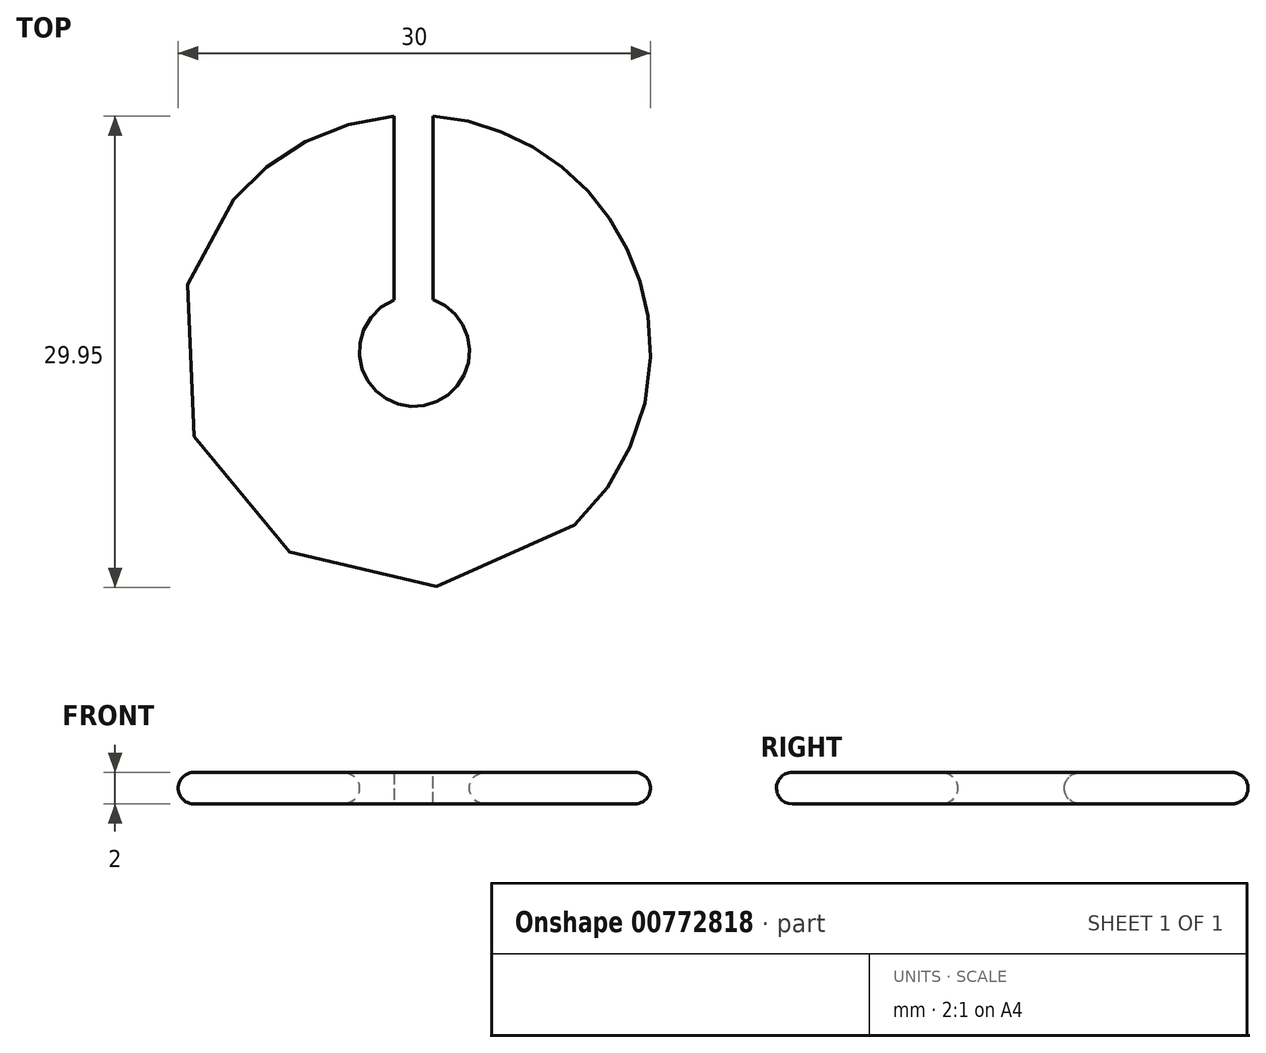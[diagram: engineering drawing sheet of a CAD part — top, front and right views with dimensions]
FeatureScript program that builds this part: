
annotation { "Feature Type Name" : "Feature", "Feature Type Description" : "" }
export const myFeature = defineFeature(function(context is Context, id is Id, definition is map)
    precondition{}
    {
        {
            var Q0;
            Q0=qCreatedBy(makeId("Top.planeOp"),FACE);
            var sketch = newSketch(context, id + "F0", { "sketchPlane" : qUnion([Q0])});
            skCircle(sketch, "E0", {"center": v(0, 0) * mm, "radius": 15 * mm});
            skCircle(sketch, "E1", {"center": v(0, 0) * mm, "radius": 3.5 * mm});
            skSolve(sketch);
        }
        {
            var Q0;
            Q0 = qSketchRegion(id + "F0", true);
            extrude(context, id + "F1", {"entities" : qUnion([Q0]), "depth" : 2 * mm, "offsetDistance" : 25 * mm});
        }
        {
            var Q0;
            Q0=makeQuery(id+"F1.opExtrude","CAP_FACE",FACE,{"disambiguationData":[OSD([sQuery(id+"F0.wireOp",EDGE,"E0"),sQuery(id+"F0.wireOp",EDGE,"E1")])],"isStart":false});
            var sketch = newSketch(context, id + "F2", { "sketchPlane" : qUnion([Q0])});
            skLineSegment(sketch, "E2.bottom", {"start": v(-1.3, 16.4) * mm, "end": v(1.2, 16.4) * mm});
            skLineSegment(sketch, "E2.top", {"start": v(-1.3, 3.21) * mm, "end": v(1.2, 3.21) * mm});
            skLineSegment(sketch, "E2.left", {"start": v(-1.3, 16.4) * mm, "end": v(-1.3, 3.21) * mm});
            skLineSegment(sketch, "E2.right", {"start": v(1.2, 16.4) * mm, "end": v(1.2, 3.21) * mm});
            skSolve(sketch);
        }
        {
            var Q0;
            {var subQ0=sQuery(id+"F2.wireOp",EDGE,"E2.left");var subQ1=makeQuery(id+"F1.opExtrude","CAP_EDGE",EDGE,{"disambiguationData":[OSD([sQuery(id+"F0.wireOp",EDGE,"E0")])],"isStart":false});var subQ2=makeQuery(id+"F2.imprint","INTERSECT",VERTEX,{"derivedFrom":[subQ1,subQ0]});Q0=makeQuery(id+"F2.imprint","IMPRINT",FACE,{"disambiguationData":[TD([[makeQuery(id+"F2.imprint","IMPRINT",EDGE,{"disambiguationData":[TD([[subQ2,-1.0]])],"derivedFrom":subQ0}),1.0]])]});}
            extrude(context, id + "F3", {"entities" : qUnion([Q0]), "operationType" : NewBodyOperationType.REMOVE, "oppositeDirection" : true, "depth" : 25 * mm, "offsetDistance" : 25 * mm});
        }
        {
            var Q0;
            Q0=makeQuery(id+"F1.opExtrude","CAP_EDGE",EDGE,{"disambiguationData":[OSD([sQuery(id+"F0.wireOp",EDGE,"E0")])],"isStart":false});
            var Q1;
            Q1=makeQuery(id+"F1.opExtrude","CAP_EDGE",EDGE,{"disambiguationData":[OSD([sQuery(id+"F0.wireOp",EDGE,"E0")])],"isStart":true});
            var Q2;
            Q2=makeQuery(id+"F1.opExtrude","CAP_EDGE",EDGE,{"disambiguationData":[OSD([sQuery(id+"F0.wireOp",EDGE,"E1")])],"isStart":false});
            var Q3;
            Q3=makeQuery(id+"F1.opExtrude","CAP_EDGE",EDGE,{"disambiguationData":[OSD([sQuery(id+"F0.wireOp",EDGE,"E1")])],"isStart":true});
            fillet(context, id + "F4", {"entities" : qUnion([Q0, Q1, Q2, Q3]), "radius" : 1 * mm, "tangentPropagation" : true, "allowEdgeOverflow" : false});
        }
    });
